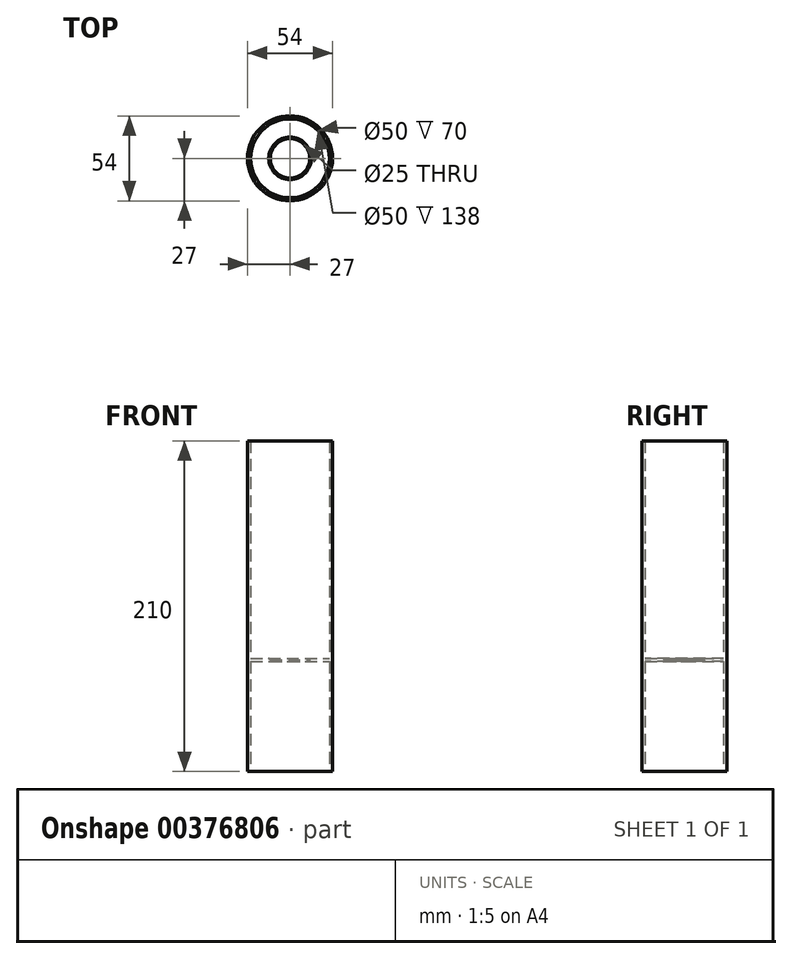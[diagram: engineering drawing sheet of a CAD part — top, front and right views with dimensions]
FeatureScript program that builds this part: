
annotation { "Feature Type Name" : "Feature", "Feature Type Description" : "" }
export const myFeature = defineFeature(function(context is Context, id is Id, definition is map)
    precondition{}
    {
        {
            var Q0;
            Q0=qCreatedBy(makeId("Front.planeOp"),FACE);
            var sketch = newSketch(context, id + "F0", { "sketchPlane" : qUnion([Q0])});
            skLineSegment(sketch, "E0", {"start": v(-27, 210) * mm, "end": v(-27, 0) * mm});
            skLineSegment(sketch, "E1", {"start": v(-27, 0) * mm, "end": v(-25, 0) * mm});
            skLineSegment(sketch, "E2", {"start": v(-25, 0) * mm, "end": v(-25, 70) * mm});
            skLineSegment(sketch, "E3", {"start": v(-25, 70) * mm, "end": v(-12.5, 70) * mm});
            skLineSegment(sketch, "E4", {"start": v(-12.5, 70) * mm, "end": v(-12.5, 71) * mm});
            skLineSegment(sketch, "E5", {"start": v(-12.5, 71) * mm, "end": v(-13.5, 72) * mm});
            skLineSegment(sketch, "E6", {"start": v(-13.5, 72) * mm, "end": v(-25, 72) * mm});
            skLineSegment(sketch, "E7", {"start": v(-25, 72) * mm, "end": v(-25, 210) * mm});
            skLineSegment(sketch, "E8", {"start": v(-25, 210) * mm, "end": v(-27, 210) * mm});
            skLineSegment(sketch, "E9", {"start": v(0, 0) * mm, "end": v(0, 210) * mm, "construction": true});
            skSolve(sketch);
        }
        {
            var Q0;
            Q0=qSketchRegion(id+"F0",true);
            var Q1;
            Q1=sQuery(id+"F0.wireOp",EDGE,"E9");
            revolve(context, id + "F1", {"entities" : qUnion([Q0]), "axis" : qUnion([Q1]), "revolveType" : RevolveType.FULL});
        }
    });
